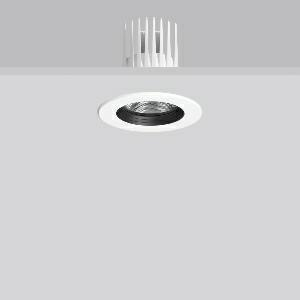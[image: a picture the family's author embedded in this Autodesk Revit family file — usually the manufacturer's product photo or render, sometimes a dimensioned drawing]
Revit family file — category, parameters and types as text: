
# Revit family: heledon_mini_e_901749_002_1_aa7d
name_source: partatom
category: Lighting Fixtures
units: mm (PartAtom-declared; Revit-internal decimal feet)

## family parameters
Cut with Voids When Loaded = No
Host = Face
Light Source = No
Part Type = Normal
Room Calculation Point = No
Round Connector Dimension = Use Diameter
Shared = No

## types (1)
- HELEDON mini E (1 x LED Modul 940, 3700 lm, 4000)
    Apparent Load = 29 VA
    Approval mark = CE
    CIE Flux Codes = 99 100 100 100 100
    Color Rendering = 92
    Color Temperature = 4000
    Default Elevation = 1800 mm
    Description = Series: HELEDON mini
Round recessed downlight. Housing: die-cast aluminium, powder-coated. Black plastic ring and recessed LED to prevent glare from the side. Optical assembly with reflector made of MIRO-Silver with 98% total light reflection for outstanding efficiency - can be changed without tools. Best colour rendering index Ra>90. Suitable for Recessed ceiling mounting. Installation without tools thanks to spring fastening system. Including separate LED converter with connecting cable 600 mm.High quality converter without flickering and stroboscopic effect. Through-wiring box (5 pole) available as accessory. The following accessories can be mounted without use of tools: interchangeable lenses, decorative glasses, honeycomb louvre, clear and frosted diffusers, white interchangeable plastic ring. 
Colour: traffic white, matt (RAL 9016)
Diameter: 124 mm
Height: 3 mm
Cut-out diameter: 114 mm
Recess height: 170 mm
Luminaire: recess height: 120 mm
Lamp: LED
Socket: without socket
Colour temperature: 4000K
Colour rendering index (CRI): 92
System power: 29 W
Rated luminous flux: 3700 lm
Luminous efficiency: 128 lm/W
Control gear: Regulated power supply
Protection class: II
Type of protection: IP 20
    Height = 0 mm  [stored 0 ft]
    Lamp = 1 x LED Modul 940
    Lamp Light Flux = 3700 lm
    Lamp count = 1
    Length = 124 mm  [stored 0.406824 ft]
    Lifetime = 50000 h
    Luminous efficacy = 128 lm/W
    Manufacturer = RZB
    ModVariant = No
    Model = 901749.002.1
    Mounting Place = Ceiling
    Mounting Type = Recessed
    Number of Poles = 1
    OnlyDefault = Yes
    Power Factor = 1
    Product Name = HELEDON mini E
    Product group = Recessed downlights
    ProductGroupID = 402
    Protection Class = Protection class II
    Protection Degree = IP 20
    RLX_Detail_Level = 1
    RLX_Emergency_Light_Flux = 0 lm
    RLX_Emergency_Type = 0
    RLX_Emergency_Type_DB = No
    RlxData = <blob elided: 127137 chars, md5=36fcea5b>
    Socket = socket
    Standby Power = 0 W
    System Light Flux = 3700 lm
    System Power = 29 W
    Type Comments = Product without accessories
    Type Image = 901657.002.jpg
    URL = http://relux.com
    VarID = ---
    Voltage = 230 V
    Voltage Range = 220-240 V
    Weight = 0.00 kg
    Width = 0 mm  [stored 0 ft]

note: [stored X ft] marks values corroborated as IEEE doubles in the binary element streams (Revit-internal decimal feet)

## geometry (parser evidence)
native form markers: Blend x4, Sweep x11
no freeform markers — native parametric forms only
